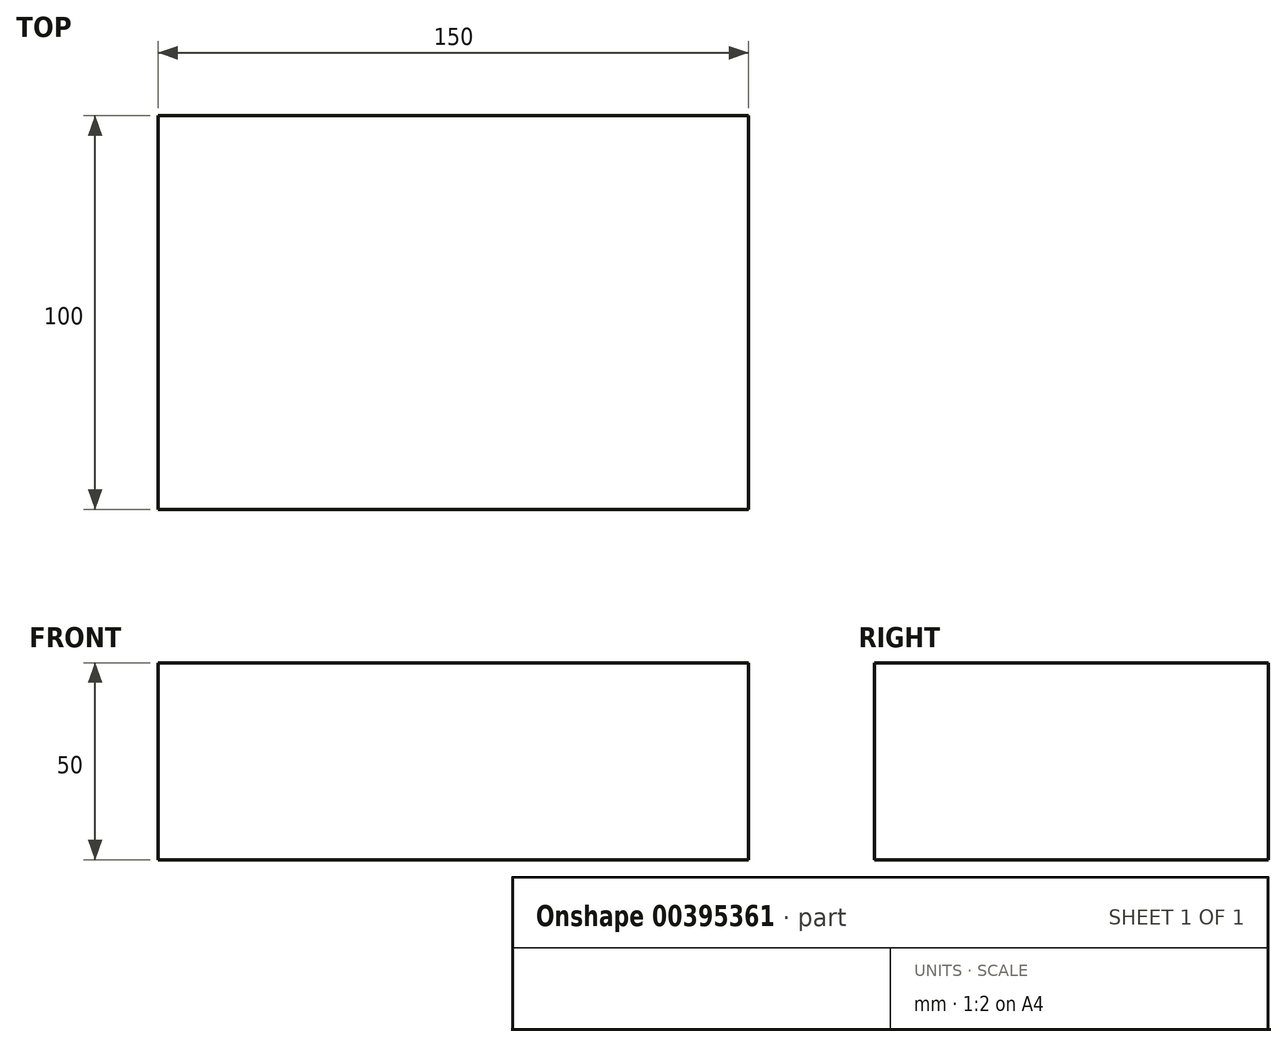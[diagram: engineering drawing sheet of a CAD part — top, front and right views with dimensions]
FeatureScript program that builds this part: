
annotation { "Feature Type Name" : "Feature", "Feature Type Description" : "" }
export const myFeature = defineFeature(function(context is Context, id is Id, definition is map)
    precondition{}
    {
        {
            var Q0;
            Q0=qCreatedBy(makeId("Top.planeOp"),FACE);
            var sketch = newSketch(context, id + "F0", { "sketchPlane" : qUnion([Q0])});
            skLineSegment(sketch, "E0.bottom", {"start": v(0, 100) * mm, "end": v(150, 100) * mm});
            skLineSegment(sketch, "E0.top", {"start": v(0, 0) * mm, "end": v(150, 0) * mm});
            skLineSegment(sketch, "E0.left", {"start": v(0, 100) * mm, "end": v(0, 0) * mm});
            skLineSegment(sketch, "E0.right", {"start": v(150, 100) * mm, "end": v(150, 0) * mm});
            skSolve(sketch);
        }
        {
            var Q0;
            Q0 = qSketchRegion(id + "F0", true);
            extrude(context, id + "F1", {"entities" : qUnion([Q0]), "depth" : 50 * mm});
        }
    });
